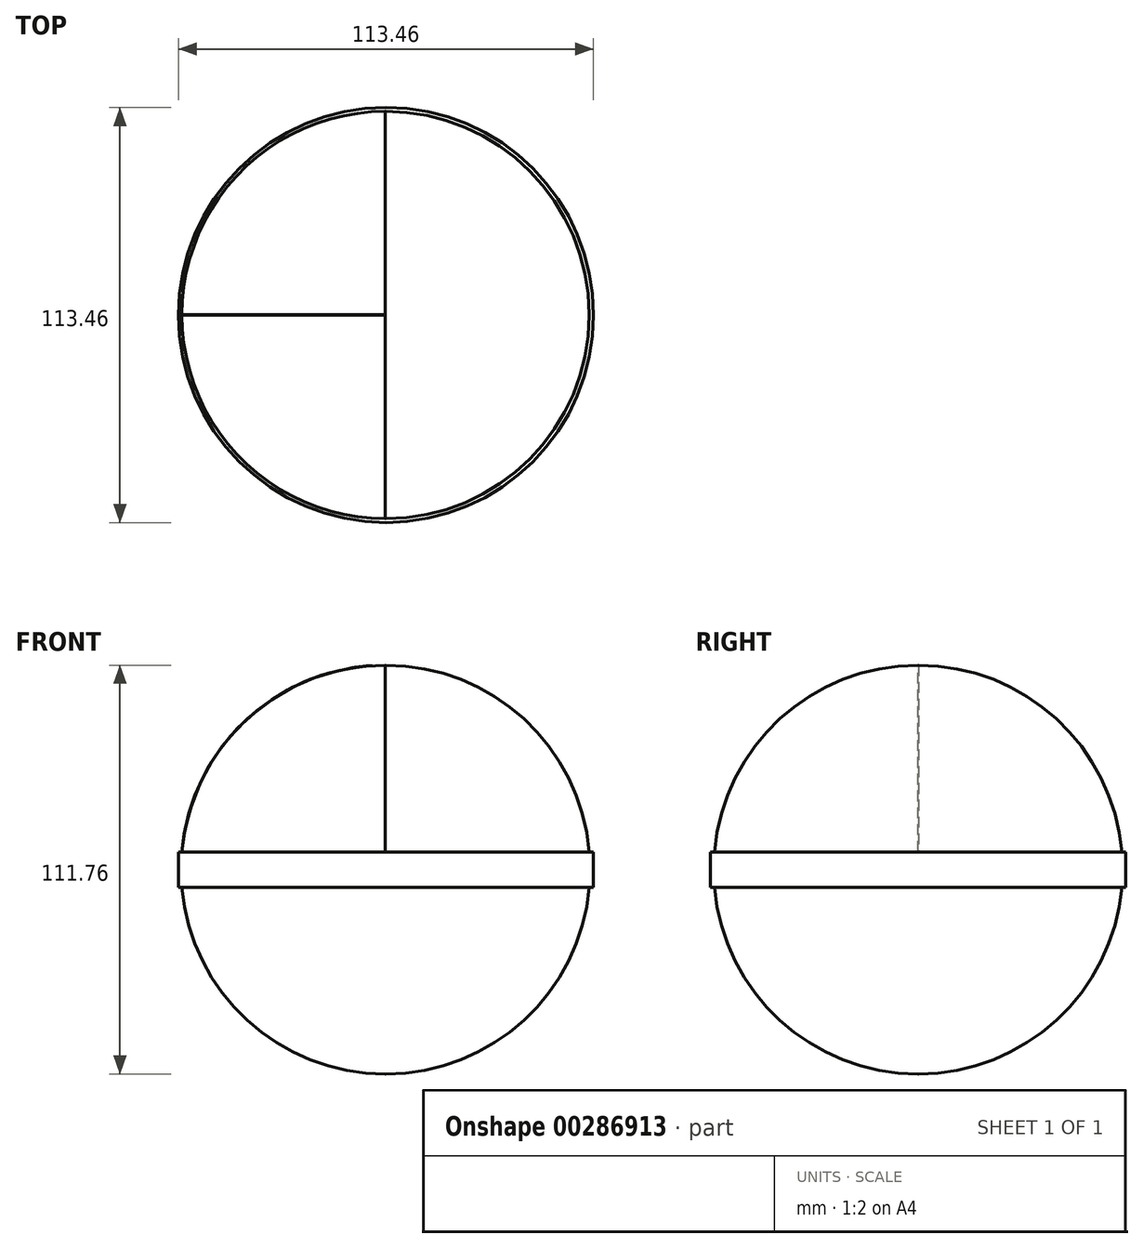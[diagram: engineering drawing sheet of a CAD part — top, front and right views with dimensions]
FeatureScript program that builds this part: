
annotation { "Feature Type Name" : "Feature", "Feature Type Description" : "" }
export const myFeature = defineFeature(function(context is Context, id is Id, definition is map)
    precondition{}
    {
        {
            var Q0;
            Q0=qCreatedBy(makeId("Front.planeOp"),FACE);
            var sketch = newSketch(context, id + "F0", { "sketchPlane" : qUnion([Q0])});
            skLineSegment(sketch, "E0.bottom", {"start": v(-56.02, 55.88) * mm, "end": v(55.74, 55.88) * mm});
            skLineSegment(sketch, "E0.top", {"start": v(-56.02, -55.88) * mm, "end": v(55.74, -55.88) * mm});
            skLineSegment(sketch, "E0.left", {"start": v(-56.02, 55.88) * mm, "end": v(-56.02, -55.88) * mm});
            skLineSegment(sketch, "E0.right", {"start": v(55.74, 55.88) * mm, "end": v(55.74, -55.88) * mm});
            skSolve(sketch);
        }
        {
            var Q0;
            Q0=makeQuery(id+"F0.imprint","IMPRINT",FACE,{"disambiguationData":[TD([[makeQuery(id+"F0.imprint","IMPRINT",EDGE,{"derivedFrom":sQuery(id+"F0.wireOp",EDGE,"E0.bottom")}),-1.0]])]});
            extrude(context, id + "F1", {"entities" : qUnion([Q0]), "endBound" : BoundingType.SYMMETRIC, "depth" : 111.76 * mm});
        }
        {
            var Q0;
            Q0=makeQuery(id+"F1.opExtrude","SWEPT_EDGE",EDGE,{"disambiguationData":[OSD([sQuery(id+"F0.wireOp",EDGE,"E0.bottom"),sQuery(id+"F0.wireOp",EDGE,"E0.left")])]});
            fillet(context, id + "F2", {"entities" : qUnion([Q0]), "radius" : 55.8 * mm, "tangentPropagation" : true, "allowEdgeOverflow" : false});
        }
        {
            var Q0;
            Q0=makeQuery(id+"F1.opExtrude","SWEPT_EDGE",EDGE,{"disambiguationData":[OSD([sQuery(id+"F0.wireOp",EDGE,"E0.bottom"),sQuery(id+"F0.wireOp",EDGE,"E0.right")])]});
            fillet(context, id + "F3", {"entities" : qUnion([Q0]), "radius" : 55.8 * mm, "tangentPropagation" : true, "allowEdgeOverflow" : false});
        }
        {
            var Q0;
            {var subQ0=sQuery(id+"F0.wireOp",EDGE,"E0.left");var subQ1=sQuery(id+"F0.wireOp",EDGE,"E0.bottom");Q0=makeQuery(id+"F2.opFillet","BLEND_EDGE",EDGE,{"blendedFrom":[makeQuery(id+"F1.opExtrude","SWEPT_EDGE",EDGE,{"disambiguationData":[OSD([subQ1,subQ0])]}),makeQuery(id+"F1.opExtrude","CAP_FACE",FACE,{"disambiguationData":[OSD([subQ1,sQuery(id+"F0.wireOp",EDGE,"E0.top"),subQ0,sQuery(id+"F0.wireOp",EDGE,"E0.right")])],"isStart":false})],"blendedInto":[makeQuery(id+"F1.opExtrude","CAP_FACE",FACE,{"disambiguationData":[OSD([subQ1,sQuery(id+"F0.wireOp",EDGE,"E0.top"),subQ0,sQuery(id+"F0.wireOp",EDGE,"E0.right")])],"isStart":false})]});}
            var Q1;
            {var subQ0=sQuery(id+"F0.wireOp",EDGE,"E0.right");var subQ1=sQuery(id+"F0.wireOp",EDGE,"E0.bottom");Q1=makeQuery(id+"F3.opFillet","BLEND_EDGE",EDGE,{"blendedFrom":[makeQuery(id+"F1.opExtrude","SWEPT_EDGE",EDGE,{"disambiguationData":[OSD([subQ1,subQ0])]}),makeQuery(id+"F1.opExtrude","CAP_FACE",FACE,{"disambiguationData":[OSD([subQ1,sQuery(id+"F0.wireOp",EDGE,"E0.top"),sQuery(id+"F0.wireOp",EDGE,"E0.left"),subQ0])],"isStart":true})],"blendedInto":[makeQuery(id+"F1.opExtrude","CAP_FACE",FACE,{"disambiguationData":[OSD([subQ1,sQuery(id+"F0.wireOp",EDGE,"E0.top"),sQuery(id+"F0.wireOp",EDGE,"E0.left"),subQ0])],"isStart":true})]});}
            fillet(context, id + "F4", {"entities" : qUnion([Q0, Q1]), "radius" : 55.8 * mm, "tangentPropagation" : true, "allowEdgeOverflow" : false});
        }
        {
            var Q0;
            Q0=makeQuery(id+"F4.opFillet","BLEND_EDGE",EDGE,{"blendedFrom":[makeQuery(id+"F1.opExtrude","CAP_EDGE",EDGE,{"disambiguationData":[OSD([sQuery(id+"F0.wireOp",EDGE,"E0.right")])],"isStart":true}),makeQuery(id+"F1.opExtrude","SWEPT_FACE",FACE,{"disambiguationData":[OSD([sQuery(id+"F0.wireOp",EDGE,"E0.top")])]})],"blendedInto":[makeQuery(id+"F1.opExtrude","SWEPT_FACE",FACE,{"disambiguationData":[OSD([sQuery(id+"F0.wireOp",EDGE,"E0.top")])]})]});
            fillet(context, id + "F5", {"entities" : qUnion([Q0]), "radius" : 55.8 * mm, "tangentPropagation" : true, "allowEdgeOverflow" : false});
        }
        {
            var Q0;
            Q0=qCreatedBy(makeId("Top.planeOp"),FACE);
            var sketch = newSketch(context, id + "F6", { "sketchPlane" : qUnion([Q0])});
            skCircle(sketch, "E1", {"center": v(0, 0) * mm, "radius": 56.73 * mm});
            skSolve(sketch);
        }
        {
            var Q0;
            Q0 = qSketchRegion(id + "F6", true);
            extrude(context, id + "F7", {"entities" : qUnion([Q0]), "operationType" : NewBodyOperationType.ADD, "endBound" : BoundingType.SYMMETRIC, "depth" : 9.65 * mm});
        }
    });
